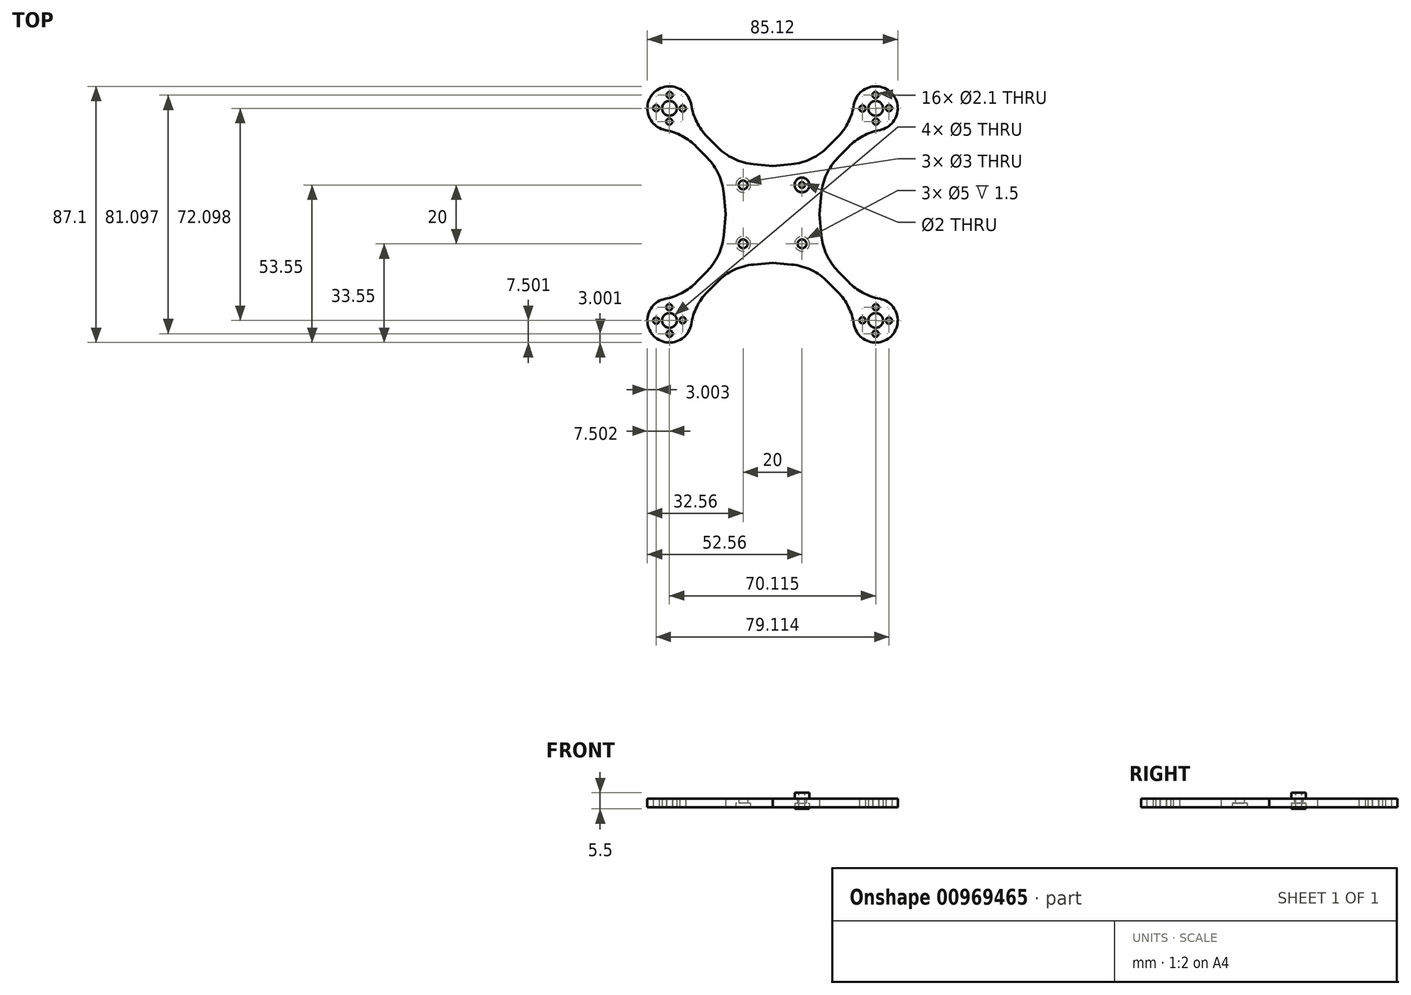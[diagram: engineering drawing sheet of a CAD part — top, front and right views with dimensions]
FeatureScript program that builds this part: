
annotation { "Feature Type Name" : "Feature", "Feature Type Description" : "" }
export const myFeature = defineFeature(function(context is Context, id is Id, definition is map)
    precondition{}
    {
        {
            var Q0;
            Q0=qCreatedBy(makeId("Top.planeOp"),FACE);
            var sketch = newSketch(context, id + "F0", { "sketchPlane" : qUnion([Q0])});
            skLineSegment(sketch, "E0.bottom", {"start": v(10, -10) * mm, "end": v(-10, -10) * mm, "construction": true});
            skLineSegment(sketch, "E0.top", {"start": v(10, 10) * mm, "end": v(-10, 10) * mm, "construction": true});
            skLineSegment(sketch, "E0.left", {"start": v(10, -10) * mm, "end": v(10, 10) * mm, "construction": true});
            skLineSegment(sketch, "E0.right", {"start": v(-10, -10) * mm, "end": v(-10, 10) * mm, "construction": true});
            skPoint(sketch, "E0.middle", {"position": v(0, 0) * mm});
            skCircle(sketch, "E1", {"center": v(-10, 10) * mm, "radius": 1.5 * mm});
            skCircle(sketch, "E2", {"center": v(10, 10) * mm, "radius": 1.5 * mm});
            skCircle(sketch, "E3", {"center": v(10, -10) * mm, "radius": 1.5 * mm});
            skCircle(sketch, "E4", {"center": v(-10, -10) * mm, "radius": 1.5 * mm});
            skCircle(sketch, "E5", {"center": v(0, 0) * mm, "radius": 50.28 * mm, "construction": true});
            skLineSegment(sketch, "E6", {"start": v(0, 0) * mm, "end": v(50.26, 51.69) * mm, "construction": true});
            skPoint(sketch, "E7", {"position": v(35.06, 36.05) * mm});
            skCircle(sketch, "E8", {"center": v(35.06, 36.05) * mm, "radius": 2.5 * mm});
            skLineSegment(sketch, "E9", {"start": v(35.06, 36.05) * mm, "end": v(35.12, 31.55) * mm, "construction": true});
            skCircle(sketch, "E10", {"center": v(35.12, 31.55) * mm, "radius": 1.05 * mm});
            skCircle(sketch, "E11.1.0", {"center": v(39.56, 36.11) * mm, "radius": 1.05 * mm});
            skCircle(sketch, "E11.2.0", {"center": v(35, 40.55) * mm, "radius": 1.05 * mm});
            skCircle(sketch, "E11.3.0", {"center": v(30.56, 35.99) * mm, "radius": 1.05 * mm});
            skCircle(sketch, "E12", {"center": v(35.06, 36.05) * mm, "radius": 7.5 * mm});
            skLineSegment(sketch, "E13.0", {"start": v(10, 6.7) * mm, "end": v(31.92, 29.24) * mm});
            skLineSegment(sketch, "E14.trimOffspring", {"start": v(35.1, 32.51) * mm, "end": v(35.19, 32.6) * mm});
            skLineSegment(sketch, "E15.trimOffspring", {"start": v(36.8, 34.26) * mm, "end": v(36.85, 34.3) * mm});
            skLineSegment(sketch, "E16.bottom", {"start": v(17.6, 18.09) * mm, "end": v(0, 16.43) * mm});
            skLineSegment(sketch, "E16.left", {"start": v(17.6, 18.09) * mm, "end": v(15.98, 0) * mm});
            skLineSegment(sketch, "E17.MirrorCS", {"start": v(6.42, 10.18) * mm, "end": v(28.34, 32.72) * mm});
            skLineSegment(sketch, "E18", {"start": v(0, 34.45) * mm, "end": v(0, -23.83) * mm, "construction": true});
            skPoint(sketch, "E18.endSnap0", {"position": v(0, -15.06) * mm});
            skLineSegment(sketch, "E19", {"start": v(38.18, 0) * mm, "end": v(-25.98, 0) * mm, "construction": true});
            skPoint(sketch, "E20.orphan", {"position": v(-14.64, 15.06) * mm});
            skPoint(sketch, "E21.orphan", {"position": v(-14.64, -15.06) * mm});
            skPoint(sketch, "E22.orphan", {"position": v(14.64, -15.06) * mm});
            skLineSegment(sketch, "E23", {"start": v(15.98, 0) * mm, "end": v(0, 0) * mm});
            skLineSegment(sketch, "E24", {"start": v(0, 16.43) * mm, "end": v(0, 0) * mm});
            skSolve(sketch);
        }
        {
            var Q0;
            Q0=makeQuery(id+"F0.imprint","IMPRINT",FACE,{"disambiguationData":[TD([[makeQuery(id+"F0.imprint","IMPRINT",EDGE,{"derivedFrom":sQuery(id+"F0.wireOp",EDGE,"E2")}),-1.0]])]});
            var Q1;
            {var subQ5=sQuery(id+"F0.wireOp",EDGE,"E13.0");var subQ6=sQuery(id+"F0.wireOp",EDGE,"E12");var subQ7=makeQuery(id+"F0.imprint","INTERSECT",VERTEX,{"derivedFrom":[subQ6,subQ5]});Q1=makeQuery(id+"F0.imprint","IMPRINT",FACE,{"disambiguationData":[TD([[makeQuery(id+"F0.imprint","IMPRINT",EDGE,{"disambiguationData":[TD([[subQ7,1.0]])],"derivedFrom":subQ6}),-1.0]])]});}
            var Q2;
            Q2=makeQuery(id+"F0.imprint","IMPRINT",FACE,{"disambiguationData":[TD([[makeQuery(id+"F0.imprint","IMPRINT",EDGE,{"derivedFrom":sQuery(id+"F0.wireOp",EDGE,"E8")}),-1.0]])]});
            extrude(context, id + "F1", {"entities" : qUnion([Q0, Q1, Q2]), "depth" : 3 * mm, "offsetDistance" : 25 * mm});
        }
        {
            var Q0;
            Q0=makeQuery(id+"F1.opExtrude","SWEPT_EDGE",EDGE,{"disambiguationData":[OSD([sQuery(id+"F0.wireOp",EDGE,"E13.0"),sQuery(id+"F0.wireOp",EDGE,"E16.left")])]});
            var Q1;
            Q1=makeQuery(id+"F1.opExtrude","SWEPT_EDGE",EDGE,{"disambiguationData":[OSD([sQuery(id+"F0.wireOp",EDGE,"E16.bottom"),sQuery(id+"F0.wireOp",EDGE,"E17.MirrorCS")])]});
            var Q2;
            Q2=makeQuery(id+"F1.opExtrude","SWEPT_EDGE",EDGE,{"disambiguationData":[OSD([sQuery(id+"F0.wireOp",EDGE,"E12"),sQuery(id+"F0.wireOp",EDGE,"E13.0")])]});
            var Q3;
            Q3=makeQuery(id+"F1.opExtrude","SWEPT_EDGE",EDGE,{"disambiguationData":[OSD([sQuery(id+"F0.wireOp",EDGE,"E12"),sQuery(id+"F0.wireOp",EDGE,"E17.MirrorCS")])]});
            fillet(context, id + "F2", {"entities" : qUnion([Q0, Q1, Q2, Q3]), "radius" : 20 * mm, "tangentPropagation" : true, "allowEdgeOverflow" : false});
        }
        {
            var Q0;
            Q0=makeQuery(id+"F1.opExtrude","CAP_FACE",FACE,{"disambiguationData":[OSD([sQuery(id+"F0.wireOp",EDGE,"E2"),sQuery(id+"F0.wireOp",EDGE,"E8"),sQuery(id+"F0.wireOp",EDGE,"E10"),sQuery(id+"F0.wireOp",EDGE,"E11.1.0"),sQuery(id+"F0.wireOp",EDGE,"E11.2.0"),sQuery(id+"F0.wireOp",EDGE,"E11.3.0"),sQuery(id+"F0.wireOp",EDGE,"E12"),sQuery(id+"F0.wireOp",EDGE,"E13.0"),sQuery(id+"F0.wireOp",EDGE,"E16.bottom"),sQuery(id+"F0.wireOp",EDGE,"E16.left"),sQuery(id+"F0.wireOp",EDGE,"E17.MirrorCS"),sQuery(id+"F0.wireOp",EDGE,"E23"),sQuery(id+"F0.wireOp",EDGE,"E24")])],"isStart":true});
            var sketch = newSketch(context, id + "F3", { "sketchPlane" : qUnion([Q0])});
            skCircle(sketch, "E25", {"center": v(10, -10) * mm, "radius": 2.5 * mm});
            skSolve(sketch);
        }
        {
            var Q0;
            Q0 = qSketchRegion(id + "F3", true);
            extrude(context, id + "F4", {"entities" : qUnion([Q0]), "operationType" : NewBodyOperationType.REMOVE, "oppositeDirection" : true, "depth" : 1.5 * mm, "offsetDistance" : 25 * mm});
        }
        {
            var Q0;
            Q0=makeQuery(id+"F1.opExtrude","SWEPT_BODY",BODY,{"disambiguationData":[OSD([sQuery(id+"F0.wireOp",EDGE,"E2"),sQuery(id+"F0.wireOp",EDGE,"E8"),sQuery(id+"F0.wireOp",EDGE,"E10"),sQuery(id+"F0.wireOp",EDGE,"E11.1.0"),sQuery(id+"F0.wireOp",EDGE,"E11.2.0"),sQuery(id+"F0.wireOp",EDGE,"E11.3.0"),sQuery(id+"F0.wireOp",EDGE,"E12"),sQuery(id+"F0.wireOp",EDGE,"E13.0"),sQuery(id+"F0.wireOp",EDGE,"E16.bottom"),sQuery(id+"F0.wireOp",EDGE,"E16.left"),sQuery(id+"F0.wireOp",EDGE,"E17.MirrorCS"),sQuery(id+"F0.wireOp",EDGE,"E23"),sQuery(id+"F0.wireOp",EDGE,"E24")])]});
            var Q1;
            Q1=qCreatedBy(makeId("Right.planeOp"),FACE);
            mirror(context, id + "F5", {"operationType" : NewBodyOperationType.ADD, "entities" : qUnion([Q0]), "mirrorPlane" : qUnion([Q1])});
        }
        {
            var Q0;
            Q0=makeQuery(id+"F1.opExtrude","SWEPT_BODY",BODY,{"disambiguationData":[OSD([sQuery(id+"F0.wireOp",EDGE,"E2"),sQuery(id+"F0.wireOp",EDGE,"E8"),sQuery(id+"F0.wireOp",EDGE,"E10"),sQuery(id+"F0.wireOp",EDGE,"E11.1.0"),sQuery(id+"F0.wireOp",EDGE,"E11.2.0"),sQuery(id+"F0.wireOp",EDGE,"E11.3.0"),sQuery(id+"F0.wireOp",EDGE,"E12"),sQuery(id+"F0.wireOp",EDGE,"E13.0"),sQuery(id+"F0.wireOp",EDGE,"E16.bottom"),sQuery(id+"F0.wireOp",EDGE,"E16.left"),sQuery(id+"F0.wireOp",EDGE,"E17.MirrorCS"),sQuery(id+"F0.wireOp",EDGE,"E23"),sQuery(id+"F0.wireOp",EDGE,"E24")])]});
            var Q1;
            Q1=qCreatedBy(makeId("Front.planeOp"),FACE);
            mirror(context, id + "F6", {"operationType" : NewBodyOperationType.ADD, "entities" : qUnion([Q0]), "mirrorPlane" : qUnion([Q1])});
        }
        {
            var Q0;
            {var subQ0=makeQuery(id+"F1.opExtrude","CAP_FACE",FACE,{"disambiguationData":[OSD([sQuery(id+"F0.wireOp",EDGE,"E2"),sQuery(id+"F0.wireOp",EDGE,"E8"),sQuery(id+"F0.wireOp",EDGE,"E10"),sQuery(id+"F0.wireOp",EDGE,"E11.1.0"),sQuery(id+"F0.wireOp",EDGE,"E11.2.0"),sQuery(id+"F0.wireOp",EDGE,"E11.3.0"),sQuery(id+"F0.wireOp",EDGE,"E12"),sQuery(id+"F0.wireOp",EDGE,"E13.0"),sQuery(id+"F0.wireOp",EDGE,"E16.bottom"),sQuery(id+"F0.wireOp",EDGE,"E16.left"),sQuery(id+"F0.wireOp",EDGE,"E17.MirrorCS"),sQuery(id+"F0.wireOp",EDGE,"E23"),sQuery(id+"F0.wireOp",EDGE,"E24")])],"isStart":false});var subQ1=makeQuery(id+"F5.boolean.opBoolean","MERGE",FACE,{"derivedFrom":[subQ0,makeQuery(id+"F5.opPattern","COPY",FACE,{"derivedFrom":subQ0,"instanceName":"1"})]});Q0=makeQuery(id+"F6.boolean.opBoolean","MERGE",FACE,{"derivedFrom":[subQ1,makeQuery(id+"F6.opPattern","COPY",FACE,{"derivedFrom":subQ1,"instanceName":"1"})]});}
            var sketch = newSketch(context, id + "F7", { "sketchPlane" : qUnion([Q0])});
            skCircle(sketch, "E26.0", {"center": v(10, 10) * mm, "radius": 1.5 * mm});
            skCircle(sketch, "E27", {"center": v(10, 10) * mm, "radius": 1 * mm});
            skSolve(sketch);
        }
        {
            var Q0;
            Q0 = qSketchRegion(id + "F7", true);
            extrude(context, id + "F8", {"entities" : qUnion([Q0]), "oppositeDirection" : true, "depth" : 1.5 * mm, "offsetDistance" : 25 * mm});
        }
        {
            var Q0;
            Q0=makeQuery(id+"F8.opExtrude","CAP_FACE",FACE,{"disambiguationData":[OSD([sQuery(id+"F7.wireOp",EDGE,"E26.0"),sQuery(id+"F7.wireOp",EDGE,"E27")])],"isStart":false});
            var sketch = newSketch(context, id + "F9", { "sketchPlane" : qUnion([Q0])});
            skCircle(sketch, "E28.0", {"center": v(10, -10) * mm, "radius": 2.5 * mm});
            skCircle(sketch, "E29.0", {"center": v(10, -10) * mm, "radius": 1.5 * mm});
            skSolve(sketch);
        }
        {
            var Q0;
            Q0 = qSketchRegion(id + "F9", true);
            var Q1;
            Q1=makeQuery(id+"F9.imprint","IMPRINT",FACE,{"disambiguationData":[TD([[makeQuery(id+"F9.imprint","IMPRINT",EDGE,{"derivedFrom":sQuery(id+"F9.wireOp",EDGE,"E29.0")}),-1.0]])]});
            extrude(context, id + "F10", {"entities" : qUnion([Q0, Q1]), "operationType" : NewBodyOperationType.ADD, "depth" : 2 * mm, "offsetDistance" : 25 * mm});
        }
        {
            var Q0;
            Q0=makeQuery(id+"F8.opExtrude","CAP_FACE",FACE,{"disambiguationData":[OSD([sQuery(id+"F7.wireOp",EDGE,"E26.0"),sQuery(id+"F7.wireOp",EDGE,"E27")])],"isStart":true});
            var sketch = newSketch(context, id + "F11", { "sketchPlane" : qUnion([Q0])});
            skCircle(sketch, "E30.0.0", {"center": v(10, 10) * mm, "radius": 2.5 * mm});
            skCircle(sketch, "E31.0", {"center": v(10, 10) * mm, "radius": 1 * mm});
            skSolve(sketch);
        }
        {
            var Q0;
            Q0 = qSketchRegion(id + "F11", true);
            extrude(context, id + "F12", {"entities" : qUnion([Q0]), "operationType" : NewBodyOperationType.ADD, "depth" : 2 * mm, "offsetDistance" : 25 * mm});
        }
    });
